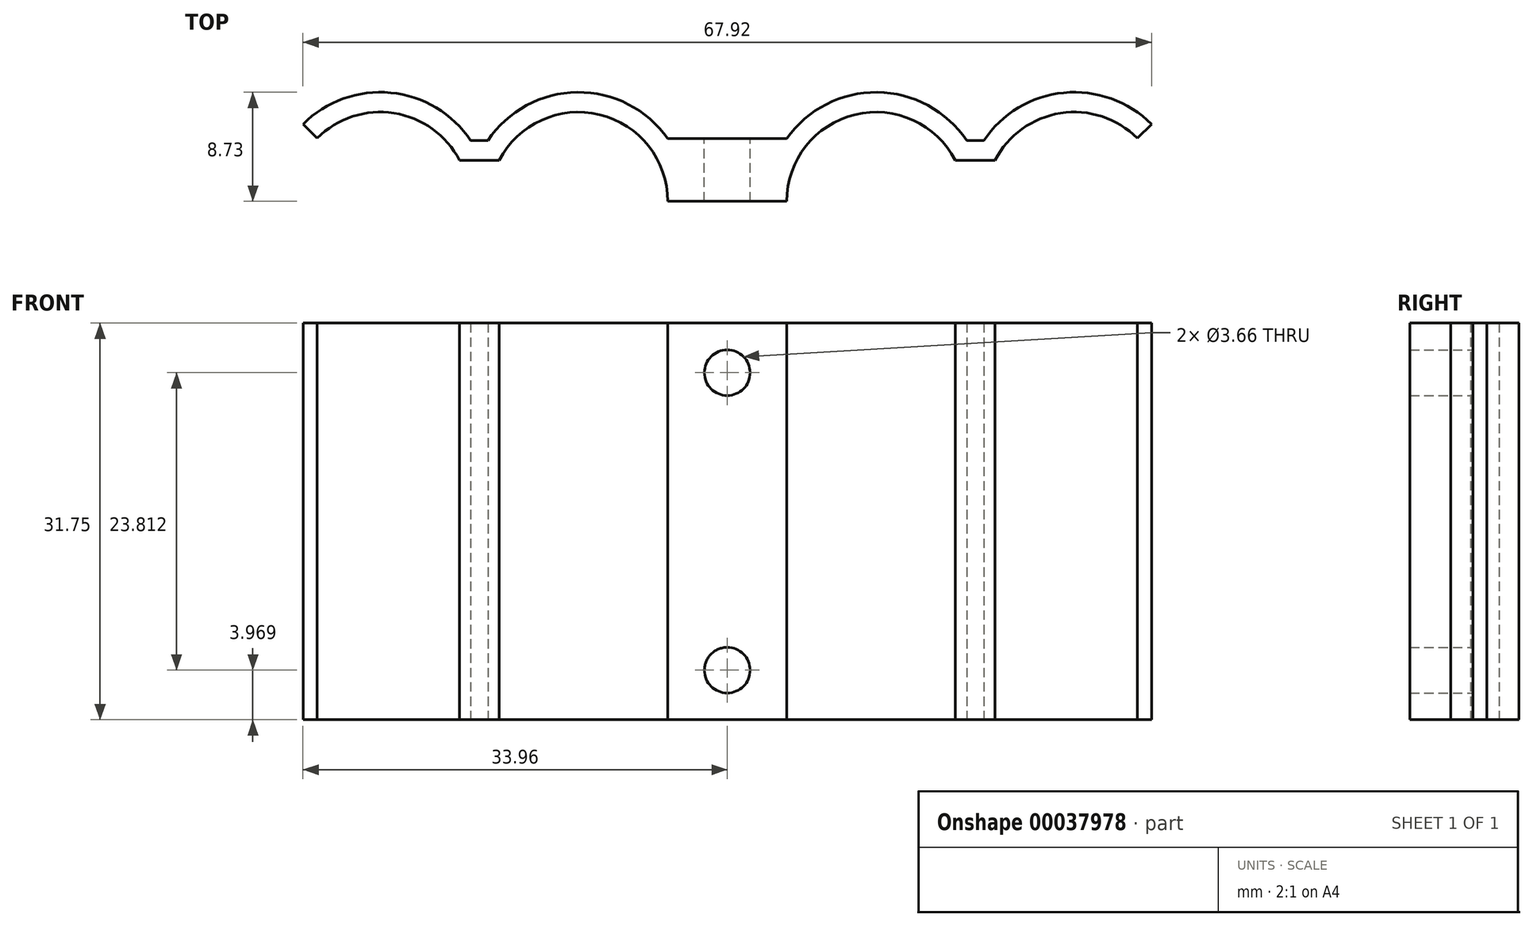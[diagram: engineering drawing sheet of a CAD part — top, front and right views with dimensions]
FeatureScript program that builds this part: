
annotation { "Feature Type Name" : "Feature", "Feature Type Description" : "" }
export const myFeature = defineFeature(function(context is Context, id is Id, definition is map)
    precondition{}
    {
        {
            var Q0;
            Q0=qCreatedBy(makeId("Top.planeOp"),FACE);
            var sketch = newSketch(context, id + "F0", { "sketchPlane" : qUnion([Q0])});
            skLineSegment(sketch, "E0", {"start": v(-4.76, 0) * mm, "end": v(4.76, 0) * mm});
            skLineSegment(sketch, "E1", {"start": v(-4.76, 0) * mm, "end": v(-11.9, 0) * mm, "construction": true});
            skLineSegment(sketch, "E2", {"start": v(4.76, 0) * mm, "end": v(11.9, 0) * mm, "construction": true});
            skArc(sketch, "E3", {"start": v(-4.76, 0) * mm, "mid": v(-10.22, 6.94) * mm, "end": v(-18.26, 3.27) * mm});
            skArc(sketch, "E4", {"start": v(18.26, 3.27) * mm, "mid": v(10.22, 6.94) * mm, "end": v(4.76, 0) * mm});
            skLineSegment(sketch, "E5", {"start": v(-11.9, 0) * mm, "end": v(-27.78, 0) * mm, "construction": true});
            skArc(sketch, "E6", {"start": v(-21.43, 3.27) * mm, "mid": v(-26.68, 7.06) * mm, "end": v(-32.83, 5.05) * mm});
            skLineSegment(sketch, "E7", {"start": v(-21.43, 3.27) * mm, "end": v(-18.26, 3.27) * mm});
            skLineSegment(sketch, "E8", {"start": v(-32.83, 5.05) * mm, "end": v(-33.96, 6.17) * mm});
            skLineSegment(sketch, "E9", {"start": v(-32.83, 5.05) * mm, "end": v(-27.78, 0) * mm, "construction": true});
            skLineSegment(sketch, "E10", {"start": v(11.9, 0) * mm, "end": v(27.78, 0) * mm, "construction": true});
            skArc(sketch, "E11", {"start": v(32.83, 5.05) * mm, "mid": v(26.68, 7.06) * mm, "end": v(21.43, 3.27) * mm});
            skLineSegment(sketch, "E12", {"start": v(18.26, 3.27) * mm, "end": v(21.43, 3.27) * mm});
            skLineSegment(sketch, "E13", {"start": v(27.78, 0) * mm, "end": v(32.83, 5.05) * mm, "construction": true});
            skLineSegment(sketch, "E14", {"start": v(32.83, 5.05) * mm, "end": v(33.96, 6.17) * mm});
            skArc(sketch, "E15", {"start": v(33.96, 6.17) * mm, "mid": v(26.93, 8.69) * mm, "end": v(20.53, 4.86) * mm});
            skArc(sketch, "E16", {"start": v(19.16, 4.86) * mm, "mid": v(12, 8.73) * mm, "end": v(4.76, 5.02) * mm});
            skLineSegment(sketch, "E17", {"start": v(4.76, 5.02) * mm, "end": v(-4.76, 5.02) * mm});
            skLineSegment(sketch, "E18", {"start": v(0, 0) * mm, "end": v(0, 5.02) * mm, "construction": true});
            skArc(sketch, "E19", {"start": v(-4.76, 5.02) * mm, "mid": v(-12, 8.73) * mm, "end": v(-19.16, 4.86) * mm});
            skArc(sketch, "E20", {"start": v(-20.53, 4.86) * mm, "mid": v(-26.93, 8.69) * mm, "end": v(-33.96, 6.17) * mm});
            skLineSegment(sketch, "E21", {"start": v(-19.16, 4.86) * mm, "end": v(-20.53, 4.86) * mm});
            skLineSegment(sketch, "E22", {"start": v(-19.84, 3.27) * mm, "end": v(-19.84, 4.86) * mm, "construction": true});
            skLineSegment(sketch, "E23", {"start": v(19.84, 3.27) * mm, "end": v(19.84, 4.86) * mm, "construction": true});
            skLineSegment(sketch, "E24", {"start": v(20.53, 4.86) * mm, "end": v(19.16, 4.86) * mm});
            skSolve(sketch);
        }
        {
            var Q0;
            Q0 = qSketchRegion(id + "F0", true);
            extrude(context, id + "F1", {"entities" : qUnion([Q0]), "depth" : 31.75 * mm});
        }
        {
            var Q0;
            Q0=makeQuery(id+"F1.opExtrude","SWEPT_FACE",FACE,{"disambiguationData":[OSD([sQuery(id+"F0.wireOp",EDGE,"E17")])]});
            var sketch = newSketch(context, id + "F2", { "sketchPlane" : qUnion([Q0])});
            skLineSegment(sketch, "E25", {"start": v(0, 31.75) * mm, "end": v(0, 27.78) * mm, "construction": true});
            skPoint(sketch, "E25.endSnap0", {"position": v(0, 31.75) * mm});
            skLineSegment(sketch, "E26", {"start": v(0, 0) * mm, "end": v(0, 3.97) * mm, "construction": true});
            skPoint(sketch, "E26.endSnap0", {"position": v(0, 0) * mm});
            skCircle(sketch, "E27", {"center": v(0, 3.97) * mm, "radius": 1.83 * mm});
            skCircle(sketch, "E28", {"center": v(0, 27.78) * mm, "radius": 1.83 * mm});
            skSolve(sketch);
        }
        {
            var Q0;
            Q0 = qSketchRegion(id + "F2", true);
            var Q1;
            Q1=makeQuery(id+"F1.opExtrude","SWEPT_FACE",FACE,{"disambiguationData":[OSD([sQuery(id+"F0.wireOp",EDGE,"E0")])]});
            extrude(context, id + "F3", {"entities" : qUnion([Q0]), "operationType" : NewBodyOperationType.REMOVE, "endBound" : BoundingType.UP_TO_SURFACE, "oppositeDirection" : true, "endBoundEntityFace" : qUnion([Q1]), "depth" : 25.4 * mm});
        }
    });
